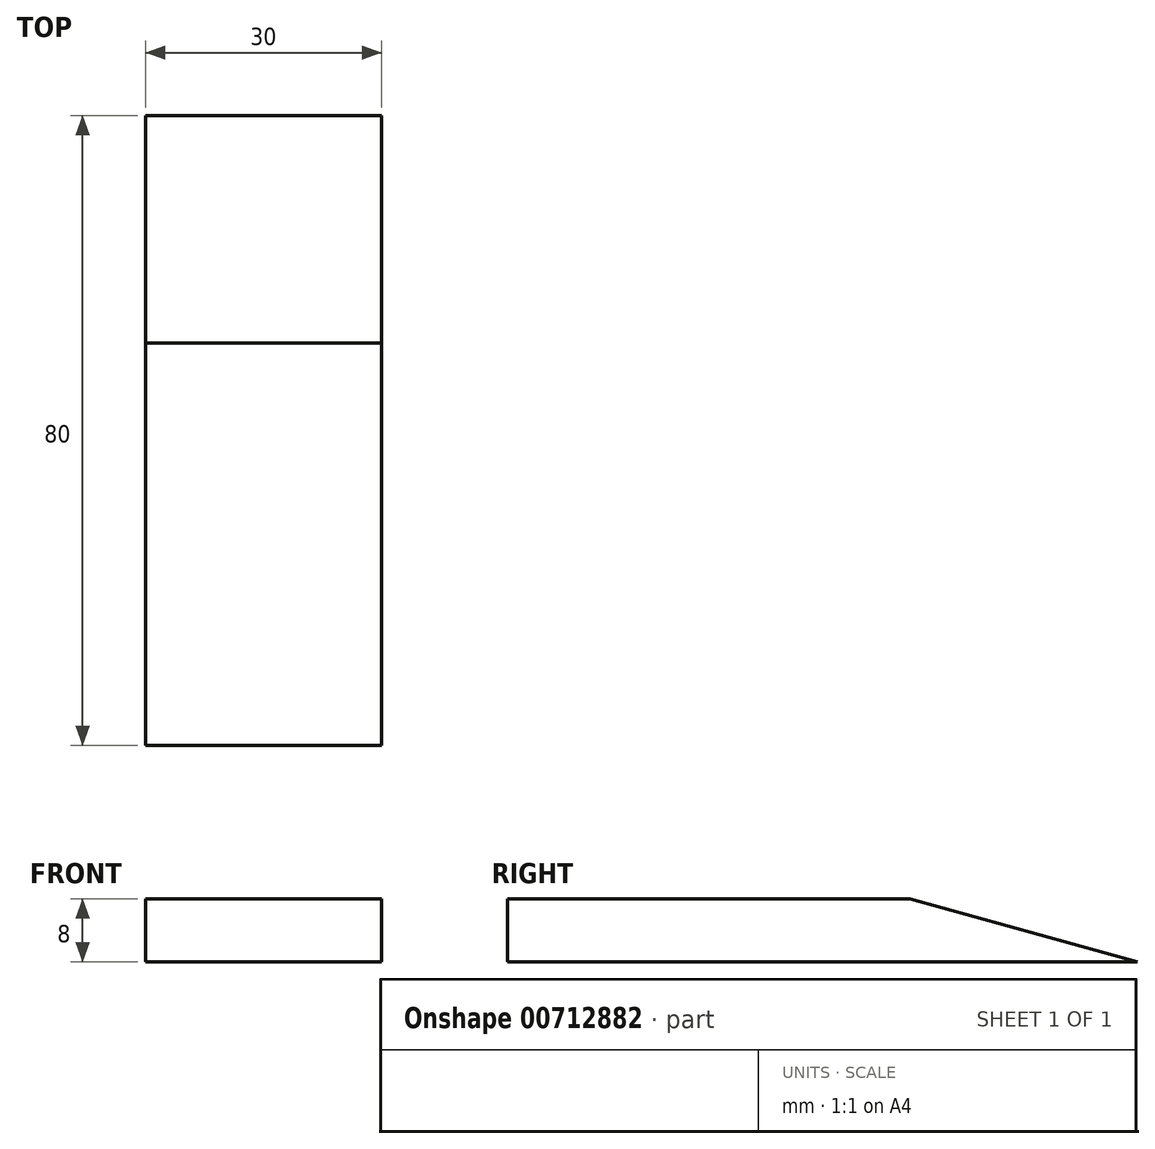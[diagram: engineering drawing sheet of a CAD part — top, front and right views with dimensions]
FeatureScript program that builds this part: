
annotation { "Feature Type Name" : "Feature", "Feature Type Description" : "" }
export const myFeature = defineFeature(function(context is Context, id is Id, definition is map)
    precondition{}
    {
        {
            var Q0;
            Q0=qCreatedBy(makeId("Right.planeOp"),FACE);
            var sketch = newSketch(context, id + "F0", { "sketchPlane" : qUnion([Q0])});
            skLineSegment(sketch, "E0", {"start": v(-25.54, -4) * mm, "end": v(-25.54, 4) * mm});
            skLineSegment(sketch, "E1", {"start": v(-25.54, 4) * mm, "end": v(25.54, 4) * mm});
            skLineSegment(sketch, "E2", {"start": v(25.54, 4) * mm, "end": v(-25.54, -4) * mm, "construction": true});
            skLineSegment(sketch, "E3", {"start": v(-25.54, -4) * mm, "end": v(54.46, -4) * mm});
            skLineSegment(sketch, "E4", {"start": v(54.46, -4) * mm, "end": v(25.54, 4) * mm});
            skSolve(sketch);
        }
        {
            var Q0;
            Q0 = qSketchRegion(id + "F0", true);
            extrude(context, id + "F1", {"entities" : qUnion([Q0]), "depth" : 30 * mm, "offsetDistance" : 25 * mm});
        }
    });
